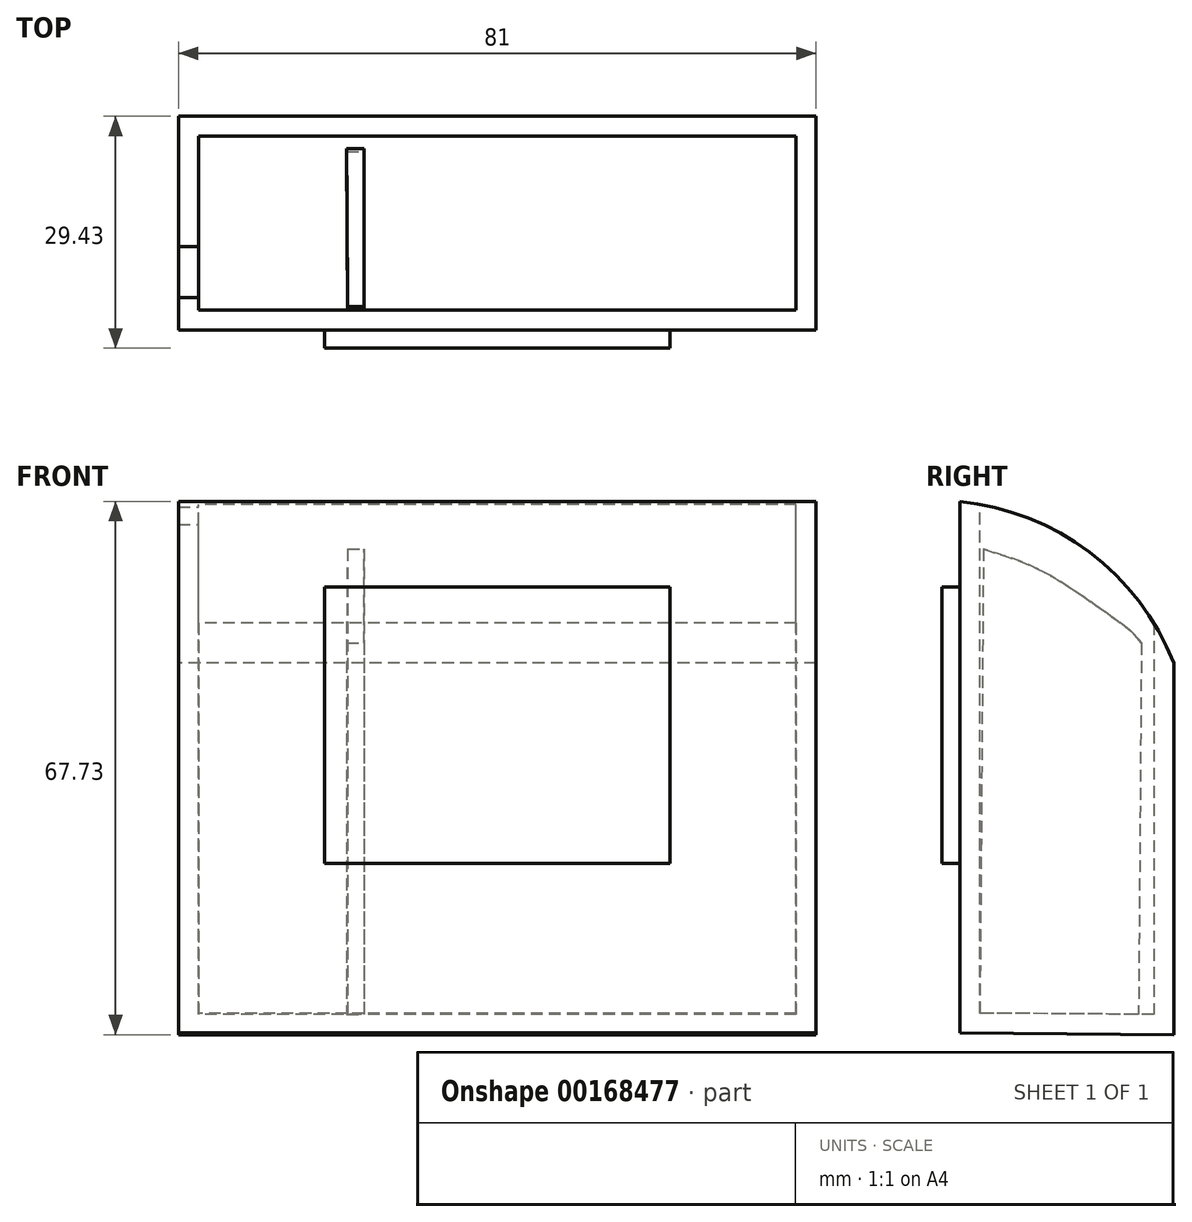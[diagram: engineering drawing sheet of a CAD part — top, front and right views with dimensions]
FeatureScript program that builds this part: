
annotation { "Feature Type Name" : "Feature", "Feature Type Description" : "" }
export const myFeature = defineFeature(function(context is Context, id is Id, definition is map)
    precondition{}
    {
        {
            var Q0;
            Q0=qCreatedBy(makeId("Right.planeOp"),FACE);
            var sketch = newSketch(context, id + "F0", { "sketchPlane" : qUnion([Q0])});
            skLineSegment(sketch, "E0", {"start": v(-42.43, -39.09) * mm, "end": v(-42.43, 28.43) * mm});
            skArc(sketch, "E1", {"start": v(-15.26, 7.94) * mm, "mid": v(-25.98, 21.98) * mm, "end": v(-42.43, 28.43) * mm});
            skLineSegment(sketch, "E2", {"start": v(-15.26, 7.94) * mm, "end": v(-15.26, -39.3) * mm});
            skLineSegment(sketch, "E3", {"start": v(-15.26, -39.3) * mm, "end": v(-42.43, -39.09) * mm});
            skSolve(sketch);
        }
        {
            var Q0;
            Q0 = qSketchRegion(id + "F0", true);
            extrude(context, id + "F1", {"entities" : qUnion([Q0]), "endBound" : BoundingType.SYMMETRIC, "depth" : 81 * mm});
        }
        {
            var Q0;
            Q0=makeQuery(id+"F1.opExtrude","SWEPT_FACE",FACE,{"disambiguationData":[OSD([sQuery(id+"F0.wireOp",EDGE,"E1")])]});
            shell(context, id + "F2", {"entities" : qUnion([Q0]), "thickness" : 2.54 * mm});
        }
        {
            var Q0;
            Q0=makeQuery(id+"F2.opShell","OFFSET_FACE",FACE,{"disambiguationData":[OSD([sQuery(id+"F0.wireOp",EDGE,"E3")])]});
            var sketch = newSketch(context, id + "F3", { "sketchPlane" : qUnion([Q0])});
            skLineSegment(sketch, "E4", {"start": v(-19.14, -19.45) * mm, "end": v(-16.94, -19.45) * mm});
            skLineSegment(sketch, "E5", {"start": v(-16.94, -19.45) * mm, "end": v(-16.94, -39.6) * mm});
            skLineSegment(sketch, "E6", {"start": v(-16.94, -39.6) * mm, "end": v(-19.02, -39.6) * mm});
            skLineSegment(sketch, "E7", {"start": v(-19.02, -39.6) * mm, "end": v(-19.14, -19.45) * mm});
            skSolve(sketch);
        }
        {
            var Q0;
            Q0 = qSketchRegion(id + "F3", true);
            extrude(context, id + "F4", {"entities" : qUnion([Q0]), "operationType" : NewBodyOperationType.ADD, "depth" : 64.65 * mm});
        }
        {
            var Q0;
            Q0=makeQuery(id+"F4.opExtrude","SWEPT_FACE",FACE,{"disambiguationData":[OSD([sQuery(id+"F3.wireOp",EDGE,"E5")])]});
            var sketch = newSketch(context, id + "F5", { "sketchPlane" : qUnion([Q0])});
            skPoint(sketch, "E8.2.internal.snap0", {"position": v(-29.31, 28) * mm});
            skFitSpline(sketch, "E8", {"points": [v(-19.33, 15.78) * mm, v(-22.8, 19.76) * mm, v(-29.31, 24.36) * mm, v(-39.4, 28.08) * mm], "startDerivative": vector(-11.43, 14.53) * mm, "endDerivative": vector(-27.15, 8.41) * mm});
            skSolve(sketch);
        }
        {
            var Q0;
            {var subQ0=sQuery(id+"F5.wireOp",EDGE,"E8");Q0=makeQuery(id+"F5.imprint","IMPRINT",FACE,{"disambiguationData":[TD([[makeQuery(id+"F5.imprint","IMPRINT",EDGE,{"derivedFrom":subQ0}),-1.0]])]});}
            extrude(context, id + "F6", {"entities" : qUnion([Q0]), "operationType" : NewBodyOperationType.REMOVE, "oppositeDirection" : true, "depth" : 25.4 * mm});
        }
        {
            var Q0;
            Q0=makeQuery(id+"F4.opExtrude","SWEPT_FACE",FACE,{"disambiguationData":[OSD([sQuery(id+"F3.wireOp",EDGE,"E5")])]});
            var sketch = newSketch(context, id + "F7", { "sketchPlane" : qUnion([Q0])});
            skFitSpline(sketch, "E9", {"points": [v(-19.37, 10.44) * mm, v(-22.06, 13) * mm, v(-32.31, 19.76) * mm, v(-39.44, 22.37) * mm], "startDerivative": vector(-12.16, 16.63) * mm, "endDerivative": vector(-20.8, 7.22) * mm});
            skSolve(sketch);
        }
        {
            var Q0;
            {var subQ0=sQuery(id+"F7.wireOp",EDGE,"E9");Q0=makeQuery(id+"F7.imprint","IMPRINT",FACE,{"disambiguationData":[TD([[makeQuery(id+"F7.imprint","IMPRINT",EDGE,{"derivedFrom":subQ0}),-1.0]])]});}
            extrude(context, id + "F8", {"entities" : qUnion([Q0]), "operationType" : NewBodyOperationType.REMOVE, "oppositeDirection" : true, "depth" : 7.84 * mm});
        }
        {
            var Q0;
            Q0=makeQuery(id+"F1.opExtrude","SWEPT_FACE",FACE,{"disambiguationData":[OSD([sQuery(id+"F0.wireOp",EDGE,"E0")])]});
            var sketch = newSketch(context, id + "F9", { "sketchPlane" : qUnion([Q0])});
            skLineSegment(sketch, "E10.bottom", {"start": v(21.95, -17.56) * mm, "end": v(-21.95, -17.56) * mm});
            skLineSegment(sketch, "E10.top", {"start": v(21.95, 17.56) * mm, "end": v(-21.95, 17.56) * mm});
            skLineSegment(sketch, "E10.left", {"start": v(21.95, -17.56) * mm, "end": v(21.95, 17.56) * mm});
            skLineSegment(sketch, "E10.right", {"start": v(-21.95, -17.56) * mm, "end": v(-21.95, 17.56) * mm});
            skPoint(sketch, "E10.middle", {"position": v(0, 0) * mm});
            skSolve(sketch);
        }
        {
            var Q0;
            Q0 = qSketchRegion(id + "F9", true);
            extrude(context, id + "F10", {"entities" : qUnion([Q0]), "depth" : 2.26 * mm});
        }
    });
